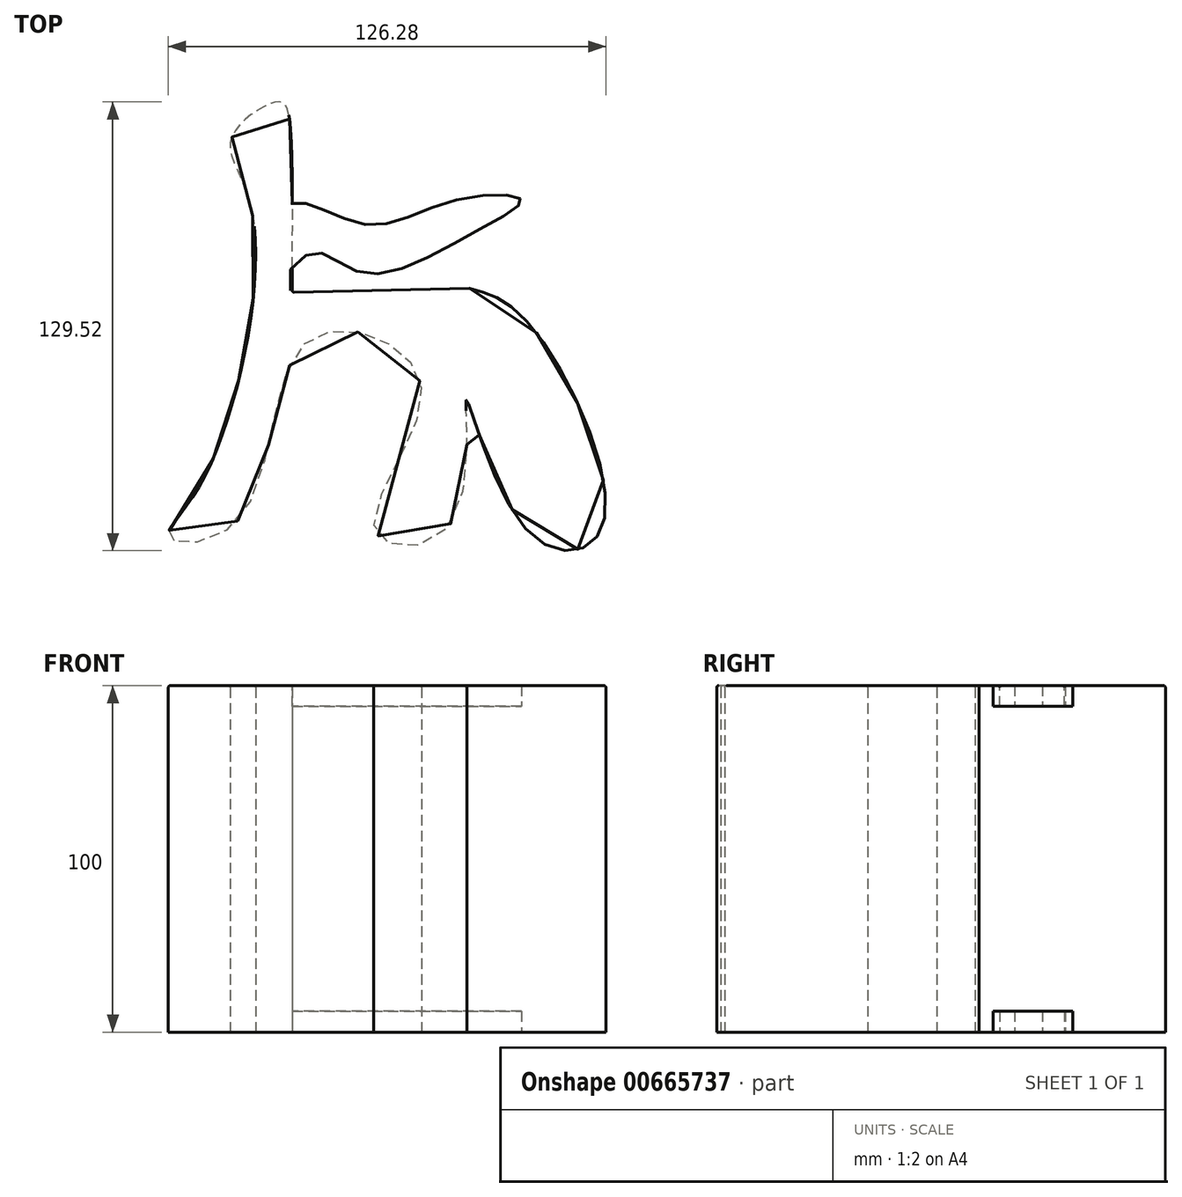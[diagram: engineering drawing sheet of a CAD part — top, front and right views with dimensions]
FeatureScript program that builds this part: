
annotation { "Feature Type Name" : "Feature", "Feature Type Description" : "" }
export const myFeature = defineFeature(function(context is Context, id is Id, definition is map)
    precondition{}
    {
        {
            var Q0;
            Q0=qCreatedBy(makeId("Top.planeOp"),FACE);
            var sketch = newSketch(context, id + "F0", { "sketchPlane" : qUnion([Q0])});
            skFitSpline(sketch, "E0", {"points": [v(-30.96, 23.58) * mm, v(-31.63, 72.75) * mm, v(-33.86, 78.34) * mm, v(-41.24, 75.88) * mm, v(-48.84, 66.5) * mm, v(-42.35, 45.7) * mm, v(-57.55, -32.07) * mm, v(-66.27, -47.5) * mm, v(-46.83, -42.58) * mm, v(-28.94, 7.04) * mm, v(-5.48, 9.95) * mm, v(6.15, -9.05) * mm, v(-6.82, -45.7) * mm, v(14.64, -43.47) * mm, v(19.33, -7.49) * mm, v(37.88, -46.15) * mm, v(58.45, -44.59) * mm, v(37.44, 14.42) * mm, v(20.23, 24.7) * mm], "startDerivative": vector(5.8, 815.07) * mm, "endDerivative": vector(-342.18, 88.18) * mm});
            skLineSegment(sketch, "E1", {"start": v(-30.96, 23.58) * mm, "end": v(20.23, 24.7) * mm});
            skSolve(sketch);
        }
        {
            var Q0;
            Q0 = qSketchRegion(id + "F0", true);
            extrude(context, id + "F1", {"entities" : qUnion([Q0]), "depth" : 50 * mm, "offsetDistance" : 25 * mm});
        }
        {
            var Q0;
            Q0=qCreatedBy(makeId("Top.planeOp"),FACE);
            cPlane(context, id + "F2", {"entities" : qUnion([Q0]), "cplaneType" : CPlaneType.OFFSET, "offset" : 50 * mm, "width" : 150 * mm, "height" : 150 * mm});
        }
        {
            var Q0;
            Q0=qCreatedBy(id+"F2.planeOp",FACE);
            var sketch = newSketch(context, id + "F3", { "sketchPlane" : qUnion([Q0])});
            skFitSpline(sketch, "E2", {"points": [v(-35.9, 44.17) * mm, v(-28, 49.43) * mm, v(-8.83, 43.04) * mm, v(16.35, 50.18) * mm, v(35.15, 50.18) * mm, v(20.11, 40.03) * mm, v(-10.71, 29.13) * mm, v(-25.75, 34.77) * mm, v(-36.27, 26.12) * mm, v(-35.9, 44.17) * mm]});
            skSolve(sketch);
        }
        {
            var Q0;
            Q0 = qSketchRegion(id + "F3", true);
            extrude(context, id + "F4", {"entities" : qUnion([Q0]), "operationType" : NewBodyOperationType.ADD, "oppositeDirection" : true, "depth" : 6 * mm, "offsetDistance" : 25 * mm});
        }
        {
            var Q0;
            Q0=makeQuery(id+"F1.opExtrude","SWEPT_BODY",BODY,{"disambiguationData":[OSD([sQuery(id+"F0.wireOp",EDGE,"E0"),sQuery(id+"F0.wireOp",EDGE,"E1")])]});
            var Q1;
            Q1=qCreatedBy(makeId("Top.planeOp"),FACE);
            mirror(context, id + "F5", {"operationType" : NewBodyOperationType.ADD, "entities" : qUnion([Q0]), "mirrorPlane" : qUnion([Q1])});
        }
        {
            var Q0;
            Q0=makeQuery(id+"F1.opExtrude","CAP_EDGE",EDGE,{"disambiguationData":[OSD([sQuery(id+"F0.wireOp",EDGE,"E0")])],"isStart":false});
            var Q1;
            Q1=makeQuery(id+"F1.opExtrude","CAP_EDGE",EDGE,{"disambiguationData":[OSD([sQuery(id+"F0.wireOp",EDGE,"E0")])],"isStart":true});
            var Q2;
            Q2=makeQuery(id+"F1.opExtrude","CAP_EDGE",EDGE,{"disambiguationData":[OSD([sQuery(id+"F0.wireOp",EDGE,"E1")])],"isStart":true});
            var Q3;
            {var subQ0=sQuery(id+"F0.wireOp",EDGE,"E1");var subQ1=sQuery(id+"F0.wireOp",EDGE,"E0");Q3=makeQuery(id+"F1.opExtrude","SWEPT_EDGE",EDGE,{"disambiguationData":[OSD([subQ1,subQ0]),TDD([makeQuery(id+"F0.imprint","INTERSECT",VERTEX,{"disambiguationData":[OD(0.0)],"derivedFrom":[subQ1,subQ0]})])]});}
            var Q4;
            {var subQ0=sQuery(id+"F0.wireOp",EDGE,"E1");var subQ1=sQuery(id+"F0.wireOp",EDGE,"E0");Q4=makeQuery(id+"F1.opExtrude","SWEPT_EDGE",EDGE,{"disambiguationData":[OSD([subQ1,subQ0]),TDD([makeQuery(id+"F0.imprint","INTERSECT",VERTEX,{"disambiguationData":[OD(1.0)],"derivedFrom":[subQ1,subQ0]})])]});}
            var Q5;
            Q5=makeQuery(id+"F1.opExtrude","CAP_EDGE",EDGE,{"disambiguationData":[OSD([sQuery(id+"F0.wireOp",EDGE,"E1")])],"isStart":false});
            fillet(context, id + "F6", {"entities" : qUnion([Q0, Q1, Q2, Q3, Q4, Q5]), "radius" : 0.5 * mm, "tangentPropagation" : true, "allowEdgeOverflow" : false});
        }
    });
